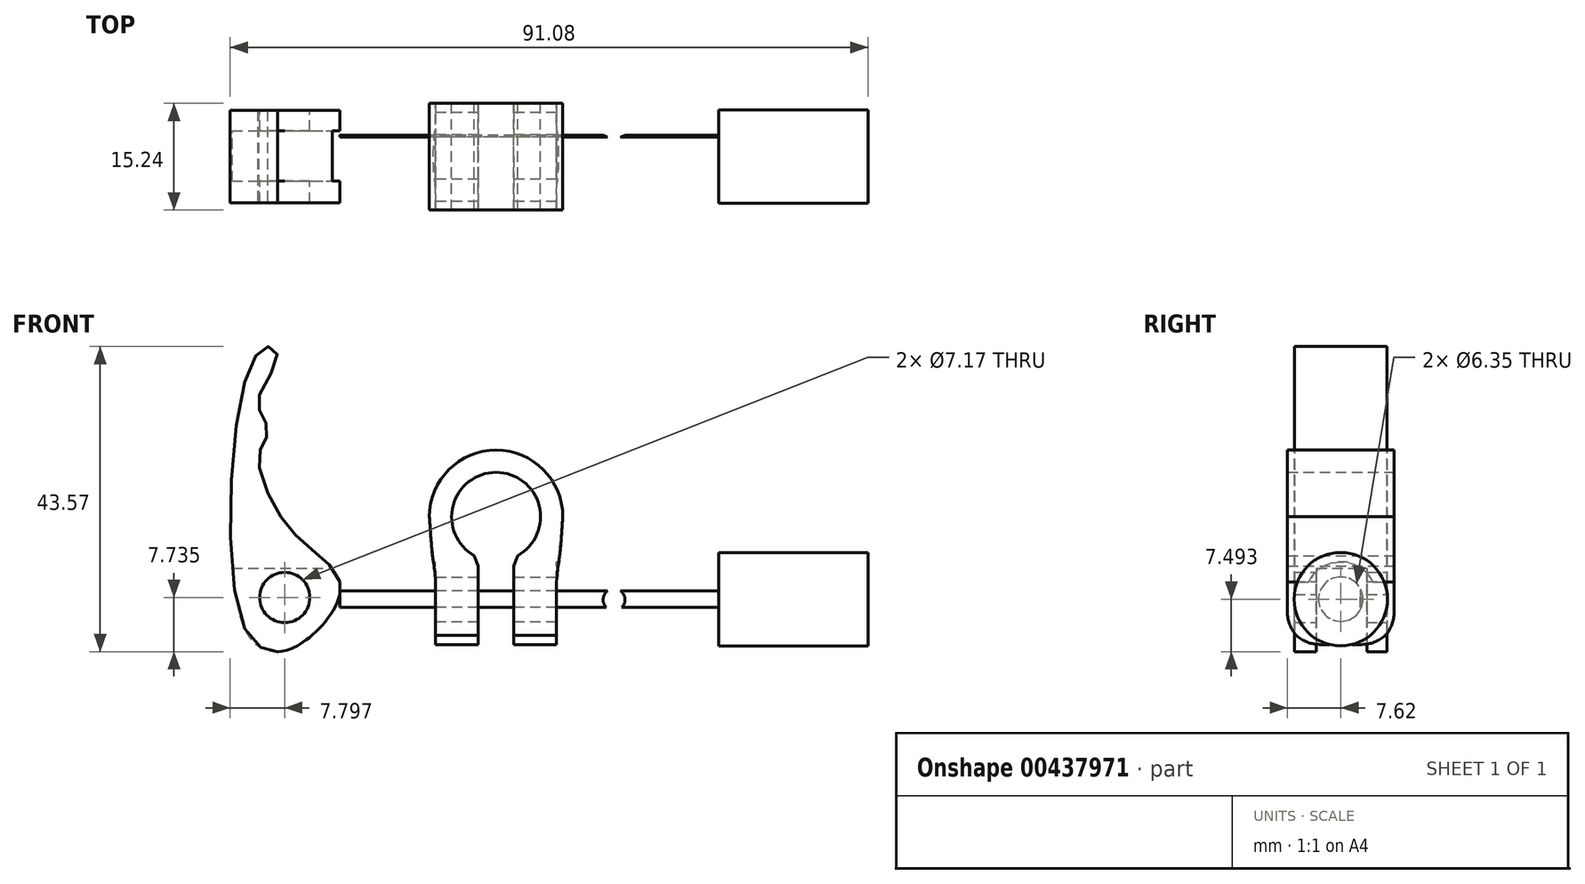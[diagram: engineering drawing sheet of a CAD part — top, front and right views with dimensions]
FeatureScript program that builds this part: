
annotation { "Feature Type Name" : "Feature", "Feature Type Description" : "" }
export const myFeature = defineFeature(function(context is Context, id is Id, definition is map)
    precondition{}
    {
        {
            var Q0;
            Q0=qCreatedBy(makeId("Front.planeOp"),FACE);
            var sketch = newSketch(context, id + "F0", { "sketchPlane" : qUnion([Q0])});
            skArc(sketch, "E0", {"start": v(3.1, -5.54) * mm, "mid": v(0, 6.35) * mm, "end": v(-3.1, -5.54) * mm});
            skArc(sketch, "E1", {"start": v(9.53, 0) * mm, "mid": v(0, 9.53) * mm, "end": v(-9.53, 0) * mm});
            skArc(sketch, "E2.MirrorC", {"start": v(-3.1, -5.54) * mm, "mid": v(0, 6.35) * mm, "end": v(3.1, -5.54) * mm});
            skArc(sketch, "E3.MirrorC", {"start": v(-9.53, 0) * mm, "mid": v(0, 9.53) * mm, "end": v(9.53, 0) * mm});
            skPoint(sketch, "E4.start.orphan", {"position": v(-9.53, 0) * mm});
            skPoint(sketch, "E5.MirrorP", {"position": v(9.53, 0) * mm});
            skLineSegment(sketch, "E6", {"start": v(-2.54, -18.23) * mm, "end": v(-2.54, -7.05) * mm});
            skLineSegment(sketch, "E7", {"start": v(-2.54, -7.05) * mm, "end": v(-3.1, -5.54) * mm});
            skFitSpline(sketch, "E8", {"points": [v(-9.53, 0) * mm, v(-9.23, -4.09) * mm, v(-8.93, -6.6) * mm, v(-8.65, -9.3) * mm, v(-8.65, -18.23) * mm], "startDerivative": vector(1.32, -14.79) * mm, "endDerivative": vector(-0.24, -15.12) * mm});
            skLineSegment(sketch, "E9", {"start": v(-8.65, -18.23) * mm, "end": v(-2.54, -18.23) * mm});
            skLineSegment(sketch, "E10", {"start": v(-8.65, -18.23) * mm, "end": v(-8.65, -9.3) * mm});
            skLineSegment(sketch, "E11.trimOffspring", {"start": v(-8.65, -18.23) * mm, "end": v(-8.65, -18.23) * mm});
            skLineSegment(sketch, "E12.MirrorCS", {"start": v(8.65, -18.23) * mm, "end": v(8.65, -9.3) * mm});
            skFitSpline(sketch, "E13.MirrorCS", {"points": [v(9.53, 0) * mm, v(9.23, -4.09) * mm, v(8.93, -6.6) * mm, v(8.65, -9.3) * mm, v(8.65, -18.23) * mm], "startDerivative": vector(-1.32, -14.79) * mm, "endDerivative": vector(0.24, -15.12) * mm});
            skLineSegment(sketch, "E14.MirrorCS", {"start": v(2.54, -18.23) * mm, "end": v(2.54, -7.05) * mm});
            skLineSegment(sketch, "E15.MirrorCS", {"start": v(8.65, -18.23) * mm, "end": v(2.54, -18.23) * mm});
            skLineSegment(sketch, "E16.MirrorCS", {"start": v(2.54, -7.05) * mm, "end": v(3.1, -5.54) * mm});
            skLineSegment(sketch, "E17.MirrorCS", {"start": v(8.65, -18.23) * mm, "end": v(8.65, -18.23) * mm});
            skSolve(sketch);
        }
        {
            var Q0;
            Q0=qSketchRegion(id+"F0",true);
            extrude(context, id + "F1", {"entities" : qUnion([Q0]), "depth" : 15.24 * mm});
        }
        {
            var Q0;
            Q0=makeQuery(id+"F1.opExtrude","SWEPT_FACE",FACE,{"disambiguationData":[OSD([sQuery(id+"F0.wireOp",EDGE,"E10")])]});
            var sketch = newSketch(context, id + "F2", { "sketchPlane" : qUnion([Q0])});
            skCircle(sketch, "E18", {"center": v(7.62, -11.51) * mm, "radius": 5.08 * mm});
            skPoint(sketch, "E19", {"position": v(7.62, -18.23) * mm});
            skSolve(sketch);
        }
        {
            var Q0;
            Q0=qSketchRegion(id+"F2",true);
            extrude(context, id + "F3", {"entities" : qUnion([Q0]), "operationType" : NewBodyOperationType.REMOVE, "depth" : 25.4 * mm});
        }
        {
            var Q0;
            Q0=makeQuery(id+"F1.opExtrude","SWEPT_FACE",FACE,{"disambiguationData":[OSD([sQuery(id+"F0.wireOp",EDGE,"E12.MirrorCS")])]});
            var sketch = newSketch(context, id + "F4", { "sketchPlane" : qUnion([Q0])});
            skCircle(sketch, "E20", {"center": v(-7.62, -11.51) * mm, "radius": 5.08 * mm});
            skPoint(sketch, "E21", {"position": v(-7.62, -18.23) * mm});
            skSolve(sketch);
        }
        {
            var Q0;
            Q0=qSketchRegion(id+"F4",true);
            extrude(context, id + "F5", {"entities" : qUnion([Q0]), "operationType" : NewBodyOperationType.REMOVE, "depth" : 25.4 * mm});
        }
        {
            var Q0;
            {var subQ0=sQuery(id+"F0.wireOp",EDGE,"E12.MirrorCS");Q0=makeQuery(id+"FgcZc90ez0dEVkm_6.boolean.opBoolean","MERGE",FACE,{"derivedFrom":[makeQuery(id+"FEB0VH3t8ekS347_6.boolean.opBoolean","MERGE",FACE,{"derivedFrom":[makeQuery(id+"F5.boolean.opBoolean","MERGE",FACE,{"derivedFrom":[makeQuery(id+"F1.opExtrude","SWEPT_FACE",FACE,{"disambiguationData":[OSD([subQ0])]}),makeQuery(id+"F5.opExtrude","CAP_FACE",FACE,{"disambiguationData":[OSD([sQuery(id+"F4.wireOp",EDGE,"E20")])],"isStart":true})]}),makeQuery(id+"FEB0VH3t8ekS347_6.opExtrude","SWEPT_FACE",FACE,{"disambiguationData":[OSD([subQ0])]})]}),makeQuery(id+"FgcZc90ez0dEVkm_6.opExtrude","SWEPT_FACE",FACE,{"disambiguationData":[OSD([subQ0])]})]});}
            var sketch = newSketch(context, id + "F6", { "sketchPlane" : qUnion([Q0])});
            skCircle(sketch, "E22", {"center": v(-7.62, -11.76) * mm, "radius": 3.18 * mm});
            skPoint(sketch, "E22.centerSnap0", {"position": v(-7.62, -18.23) * mm});
            skSolve(sketch);
        }
        {
            var Q0;
            Q0=qSketchRegion(id+"F6",true);
            extrude(context, id + "F7", {"entities" : qUnion([Q0]), "operationType" : NewBodyOperationType.REMOVE, "oppositeDirection" : true, "depth" : 25.4 * mm});
        }
        {
            var Q0;
            Q0=makeQuery(id+"F1.opExtrude","CAP_EDGE",EDGE,{"disambiguationData":[OSD([sQuery(id+"F0.wireOp",EDGE,"E15.MirrorCS")])],"isStart":false});
            var Q1;
            Q1=makeQuery(id+"F1.opExtrude","CAP_EDGE",EDGE,{"disambiguationData":[OSD([sQuery(id+"F0.wireOp",EDGE,"E15.MirrorCS")])],"isStart":true});
            var Q2;
            Q2=makeQuery(id+"F1.opExtrude","CAP_EDGE",EDGE,{"disambiguationData":[OSD([sQuery(id+"F0.wireOp",EDGE,"E9")])],"isStart":false});
            var Q3;
            Q3=makeQuery(id+"F1.opExtrude","CAP_EDGE",EDGE,{"disambiguationData":[OSD([sQuery(id+"F0.wireOp",EDGE,"E9")])],"isStart":true});
            chamfer(context, id + "F8", {"entities" : qUnion([Q0, Q1, Q2, Q3]), "width" : 2.54 * mm, "tangentPropagation" : true});
        }
        {
            var Q0;
            {var subQ0=sQuery(id+"F0.wireOp",EDGE,"E9");Q0=makeQuery(id+"F8.opChamfer","BLEND_EDGE",EDGE,{"blendedFrom":[makeQuery(id+"F1.opExtrude","CAP_EDGE",EDGE,{"disambiguationData":[OSD([subQ0])],"isStart":false}),makeQuery(id+"F1.opExtrude","CAP_FACE",FACE,{"disambiguationData":[OSD([sQuery(id+"F0.wireOp",EDGE,"E0"),sQuery(id+"F0.wireOp",EDGE,"E1"),sQuery(id+"F0.wireOp",EDGE,"E6"),sQuery(id+"F0.wireOp",EDGE,"E7"),sQuery(id+"F0.wireOp",EDGE,"E8"),subQ0,sQuery(id+"F0.wireOp",EDGE,"E10"),sQuery(id+"F0.wireOp",EDGE,"E12.MirrorCS"),sQuery(id+"F0.wireOp",EDGE,"E13.MirrorCS"),sQuery(id+"F0.wireOp",EDGE,"E14.MirrorCS"),sQuery(id+"F0.wireOp",EDGE,"E15.MirrorCS"),sQuery(id+"F0.wireOp",EDGE,"E16.MirrorCS")])],"isStart":false})],"blendedInto":[makeQuery(id+"F1.opExtrude","CAP_FACE",FACE,{"disambiguationData":[OSD([sQuery(id+"F0.wireOp",EDGE,"E0"),sQuery(id+"F0.wireOp",EDGE,"E1"),sQuery(id+"F0.wireOp",EDGE,"E6"),sQuery(id+"F0.wireOp",EDGE,"E7"),sQuery(id+"F0.wireOp",EDGE,"E8"),subQ0,sQuery(id+"F0.wireOp",EDGE,"E10"),sQuery(id+"F0.wireOp",EDGE,"E12.MirrorCS"),sQuery(id+"F0.wireOp",EDGE,"E13.MirrorCS"),sQuery(id+"F0.wireOp",EDGE,"E14.MirrorCS"),sQuery(id+"F0.wireOp",EDGE,"E15.MirrorCS"),sQuery(id+"F0.wireOp",EDGE,"E16.MirrorCS")])],"isStart":false})]});}
            var Q1;
            {var subQ0=sQuery(id+"F0.wireOp",EDGE,"E9");Q1=makeQuery(id+"F8.opChamfer","BLEND_EDGE",EDGE,{"blendedFrom":[makeQuery(id+"F1.opExtrude","CAP_EDGE",EDGE,{"disambiguationData":[OSD([subQ0])],"isStart":false}),makeQuery(id+"F1.opExtrude","SWEPT_FACE",FACE,{"disambiguationData":[OSD([subQ0])]})],"blendedInto":[makeQuery(id+"F1.opExtrude","SWEPT_FACE",FACE,{"disambiguationData":[OSD([subQ0])]})]});}
            var Q2;
            {var subQ0=sQuery(id+"F0.wireOp",EDGE,"E9");Q2=makeQuery(id+"F8.opChamfer","BLEND_EDGE",EDGE,{"blendedFrom":[makeQuery(id+"F1.opExtrude","CAP_EDGE",EDGE,{"disambiguationData":[OSD([subQ0])],"isStart":true}),makeQuery(id+"F1.opExtrude","SWEPT_FACE",FACE,{"disambiguationData":[OSD([subQ0])]})],"blendedInto":[makeQuery(id+"F1.opExtrude","SWEPT_FACE",FACE,{"disambiguationData":[OSD([subQ0])]})]});}
            var Q3;
            {var subQ0=sQuery(id+"F0.wireOp",EDGE,"E9");Q3=makeQuery(id+"F8.opChamfer","BLEND_EDGE",EDGE,{"blendedFrom":[makeQuery(id+"F1.opExtrude","CAP_EDGE",EDGE,{"disambiguationData":[OSD([subQ0])],"isStart":true}),makeQuery(id+"F1.opExtrude","CAP_FACE",FACE,{"disambiguationData":[OSD([sQuery(id+"F0.wireOp",EDGE,"E0"),sQuery(id+"F0.wireOp",EDGE,"E1"),sQuery(id+"F0.wireOp",EDGE,"E6"),sQuery(id+"F0.wireOp",EDGE,"E7"),sQuery(id+"F0.wireOp",EDGE,"E8"),subQ0,sQuery(id+"F0.wireOp",EDGE,"E10"),sQuery(id+"F0.wireOp",EDGE,"E12.MirrorCS"),sQuery(id+"F0.wireOp",EDGE,"E13.MirrorCS"),sQuery(id+"F0.wireOp",EDGE,"E14.MirrorCS"),sQuery(id+"F0.wireOp",EDGE,"E15.MirrorCS"),sQuery(id+"F0.wireOp",EDGE,"E16.MirrorCS")])],"isStart":true})],"blendedInto":[makeQuery(id+"F1.opExtrude","CAP_FACE",FACE,{"disambiguationData":[OSD([sQuery(id+"F0.wireOp",EDGE,"E0"),sQuery(id+"F0.wireOp",EDGE,"E1"),sQuery(id+"F0.wireOp",EDGE,"E6"),sQuery(id+"F0.wireOp",EDGE,"E7"),sQuery(id+"F0.wireOp",EDGE,"E8"),subQ0,sQuery(id+"F0.wireOp",EDGE,"E10"),sQuery(id+"F0.wireOp",EDGE,"E12.MirrorCS"),sQuery(id+"F0.wireOp",EDGE,"E13.MirrorCS"),sQuery(id+"F0.wireOp",EDGE,"E14.MirrorCS"),sQuery(id+"F0.wireOp",EDGE,"E15.MirrorCS"),sQuery(id+"F0.wireOp",EDGE,"E16.MirrorCS")])],"isStart":true})]});}
            var Q4;
            {var subQ0=sQuery(id+"F0.wireOp",EDGE,"E15.MirrorCS");Q4=makeQuery(id+"F8.opChamfer","BLEND_EDGE",EDGE,{"blendedFrom":[makeQuery(id+"F1.opExtrude","CAP_EDGE",EDGE,{"disambiguationData":[OSD([subQ0])],"isStart":true}),makeQuery(id+"F1.opExtrude","CAP_FACE",FACE,{"disambiguationData":[OSD([sQuery(id+"F0.wireOp",EDGE,"E0"),sQuery(id+"F0.wireOp",EDGE,"E1"),sQuery(id+"F0.wireOp",EDGE,"E6"),sQuery(id+"F0.wireOp",EDGE,"E7"),sQuery(id+"F0.wireOp",EDGE,"E8"),sQuery(id+"F0.wireOp",EDGE,"E9"),sQuery(id+"F0.wireOp",EDGE,"E10"),sQuery(id+"F0.wireOp",EDGE,"E12.MirrorCS"),sQuery(id+"F0.wireOp",EDGE,"E13.MirrorCS"),sQuery(id+"F0.wireOp",EDGE,"E14.MirrorCS"),subQ0,sQuery(id+"F0.wireOp",EDGE,"E16.MirrorCS")])],"isStart":true})],"blendedInto":[makeQuery(id+"F1.opExtrude","CAP_FACE",FACE,{"disambiguationData":[OSD([sQuery(id+"F0.wireOp",EDGE,"E0"),sQuery(id+"F0.wireOp",EDGE,"E1"),sQuery(id+"F0.wireOp",EDGE,"E6"),sQuery(id+"F0.wireOp",EDGE,"E7"),sQuery(id+"F0.wireOp",EDGE,"E8"),sQuery(id+"F0.wireOp",EDGE,"E9"),sQuery(id+"F0.wireOp",EDGE,"E10"),sQuery(id+"F0.wireOp",EDGE,"E12.MirrorCS"),sQuery(id+"F0.wireOp",EDGE,"E13.MirrorCS"),sQuery(id+"F0.wireOp",EDGE,"E14.MirrorCS"),subQ0,sQuery(id+"F0.wireOp",EDGE,"E16.MirrorCS")])],"isStart":true})]});}
            var Q5;
            {var subQ0=sQuery(id+"F0.wireOp",EDGE,"E15.MirrorCS");Q5=makeQuery(id+"F8.opChamfer","BLEND_EDGE",EDGE,{"blendedFrom":[makeQuery(id+"F1.opExtrude","CAP_EDGE",EDGE,{"disambiguationData":[OSD([subQ0])],"isStart":true}),makeQuery(id+"F1.opExtrude","SWEPT_FACE",FACE,{"disambiguationData":[OSD([subQ0])]})],"blendedInto":[makeQuery(id+"F1.opExtrude","SWEPT_FACE",FACE,{"disambiguationData":[OSD([subQ0])]})]});}
            var Q6;
            {var subQ0=sQuery(id+"F0.wireOp",EDGE,"E15.MirrorCS");Q6=makeQuery(id+"F8.opChamfer","BLEND_EDGE",EDGE,{"blendedFrom":[makeQuery(id+"F1.opExtrude","CAP_EDGE",EDGE,{"disambiguationData":[OSD([subQ0])],"isStart":false}),makeQuery(id+"F1.opExtrude","SWEPT_FACE",FACE,{"disambiguationData":[OSD([subQ0])]})],"blendedInto":[makeQuery(id+"F1.opExtrude","SWEPT_FACE",FACE,{"disambiguationData":[OSD([subQ0])]})]});}
            var Q7;
            {var subQ0=sQuery(id+"F0.wireOp",EDGE,"E15.MirrorCS");Q7=makeQuery(id+"F8.opChamfer","BLEND_EDGE",EDGE,{"blendedFrom":[makeQuery(id+"F1.opExtrude","CAP_EDGE",EDGE,{"disambiguationData":[OSD([subQ0])],"isStart":false}),makeQuery(id+"F1.opExtrude","CAP_FACE",FACE,{"disambiguationData":[OSD([sQuery(id+"F0.wireOp",EDGE,"E0"),sQuery(id+"F0.wireOp",EDGE,"E1"),sQuery(id+"F0.wireOp",EDGE,"E6"),sQuery(id+"F0.wireOp",EDGE,"E7"),sQuery(id+"F0.wireOp",EDGE,"E8"),sQuery(id+"F0.wireOp",EDGE,"E9"),sQuery(id+"F0.wireOp",EDGE,"E10"),sQuery(id+"F0.wireOp",EDGE,"E12.MirrorCS"),sQuery(id+"F0.wireOp",EDGE,"E13.MirrorCS"),sQuery(id+"F0.wireOp",EDGE,"E14.MirrorCS"),subQ0,sQuery(id+"F0.wireOp",EDGE,"E16.MirrorCS")])],"isStart":false})],"blendedInto":[makeQuery(id+"F1.opExtrude","CAP_FACE",FACE,{"disambiguationData":[OSD([sQuery(id+"F0.wireOp",EDGE,"E0"),sQuery(id+"F0.wireOp",EDGE,"E1"),sQuery(id+"F0.wireOp",EDGE,"E6"),sQuery(id+"F0.wireOp",EDGE,"E7"),sQuery(id+"F0.wireOp",EDGE,"E8"),sQuery(id+"F0.wireOp",EDGE,"E9"),sQuery(id+"F0.wireOp",EDGE,"E10"),sQuery(id+"F0.wireOp",EDGE,"E12.MirrorCS"),sQuery(id+"F0.wireOp",EDGE,"E13.MirrorCS"),sQuery(id+"F0.wireOp",EDGE,"E14.MirrorCS"),subQ0,sQuery(id+"F0.wireOp",EDGE,"E16.MirrorCS")])],"isStart":false})]});}
            fillet(context, id + "F9", {"entities" : qUnion([Q0, Q1, Q2, Q3, Q4, Q5, Q6, Q7]), "radius" : 5.08 * mm, "tangentPropagation" : true, "allowEdgeOverflow" : false});
        }
        {
            var Q0;
            Q0=makeQuery(id+"F5.boolean.opBoolean","MERGE",FACE,{"derivedFrom":[makeQuery(id+"F1.opExtrude","SWEPT_FACE",FACE,{"disambiguationData":[OSD([sQuery(id+"F0.wireOp",EDGE,"E12.MirrorCS")])]}),makeQuery(id+"F5.opExtrude","CAP_FACE",FACE,{"disambiguationData":[OSD([sQuery(id+"F4.wireOp",EDGE,"E20")])],"isStart":true})]});
            var sketch = newSketch(context, id + "F10", { "sketchPlane" : qUnion([Q0])});
            skCircle(sketch, "E23", {"center": v(-7.62, -11.76) * mm, "radius": 3.05 * mm});
            skLineSegment(sketch, "E24", {"start": v(-4.81, -10.57) * mm, "end": v(-4.81, -13.24) * mm});
            skSolve(sketch);
        }
        {
            var Q0;
            {var subQ0=sQuery(id+"F10.wireOp",EDGE,"E24");var subQ1=sQuery(id+"F10.wireOp",EDGE,"E23");var subQ2=makeQuery(id+"F10.imprint","INTERSECT",VERTEX,{"disambiguationData":[OD(0.0)],"derivedFrom":[subQ1,subQ0]});Q0=makeQuery(id+"F10.imprint","IMPRINT",FACE,{"disambiguationData":[TD([[makeQuery(id+"F10.imprint","IMPRINT",EDGE,{"disambiguationData":[TD([[subQ2,-1.0]])],"derivedFrom":subQ1}),1.0]])]});}
            extrude(context, id + "F11", {"entities" : qUnion([Q0]), "depth" : 44.45 * mm});
        }
        {
            var Q0;
            Q0=makeQuery(id+"F11.opExtrude","CAP_FACE",FACE,{"disambiguationData":[OSD([sQuery(id+"F10.wireOp",EDGE,"E23")])],"isStart":true});
            extrude(context, id + "F12", {"entities" : qUnion([Q0]), "operationType" : NewBodyOperationType.ADD, "depth" : 30.99 * mm});
        }
        {
            var Q0;
            Q0=makeQuery(id+"F12.opExtrude","CAP_FACE",FACE,{"disambiguationData":[OSD([sQuery(id+"F10.wireOp",EDGE,"E23")])],"isStart":false});
            var sketch = newSketch(context, id + "F13", { "sketchPlane" : qUnion([Q0])});
            skLineSegment(sketch, "E25.bottom", {"start": v(1.02, 24.95) * mm, "end": v(14.22, 24.95) * mm});
            skLineSegment(sketch, "E25.top", {"start": v(1.02, -19.25) * mm, "end": v(14.22, -19.25) * mm});
            skLineSegment(sketch, "E25.left", {"start": v(1.02, 24.95) * mm, "end": v(1.02, -19.25) * mm});
            skLineSegment(sketch, "E25.right", {"start": v(14.22, 24.95) * mm, "end": v(14.22, -19.25) * mm});
            skLineSegment(sketch, "E26.bottom", {"start": v(3.9, -19.25) * mm, "end": v(11.12, -19.25) * mm});
            skLineSegment(sketch, "E26.top", {"start": v(3.9, -7.36) * mm, "end": v(11.12, -7.36) * mm});
            skLineSegment(sketch, "E26.left", {"start": v(3.9, -19.25) * mm, "end": v(3.9, -7.36) * mm});
            skLineSegment(sketch, "E26.right", {"start": v(11.12, -19.25) * mm, "end": v(11.12, -7.36) * mm});
            skSolve(sketch);
        }
        {
            var Q0;
            Q0=makeQuery(id+"F13.imprint","IMPRINT",FACE,{"disambiguationData":[TD([[makeQuery(id+"F13.imprint","IMPRINT",EDGE,{"derivedFrom":sQuery(id+"F13.wireOp",EDGE,"E25.bottom")}),-1.0]])]});
            extrude(context, id + "F14", {"entities" : qUnion([Q0]), "depth" : 17.78 * mm});
        }
        {
            var Q0;
            Q0=makeQuery(id+"F14.opExtrude","SWEPT_FACE",FACE,{"disambiguationData":[OSD([sQuery(id+"F13.wireOp",EDGE,"E25.left")])]});
            var sketch = newSketch(context, id + "F15", { "sketchPlane" : qUnion([Q0])});
            skPoint(sketch, "E27.5.internal.snap0", {"position": v(31.23, -19.25) * mm});
            skPoint(sketch, "E27.10.internal.snap0", {"position": v(31.23, -19.25) * mm});
            skFitSpline(sketch, "E27", {"points": [v(31.23, -19.25) * mm, v(28.62, -18.54) * mm, v(24.27, -14.84) * mm, v(22.34, -9.26) * mm, v(26.41, -4.6) * mm, v(31.23, 0.78) * mm, v(33.89, 8.88) * mm, v(32.77, 11.32) * mm, v(33.19, 14.19) * mm, v(34.02, 16.77) * mm, v(31.23, 22.99) * mm, v(32.63, 24.32) * mm, v(36.33, 17.47) * mm, v(35.7, -16.4) * mm, v(31.23, -19.25) * mm]});
            skCircle(sketch, "E28", {"center": v(30.18, -11.52) * mm, "radius": 3.58 * mm});
            skLineSegment(sketch, "E29", {"start": v(29.96, -5.35) * mm, "end": v(33.78, -2.43) * mm});
            skLineSegment(sketch, "E30", {"start": v(33.78, -2.43) * mm, "end": v(33.78, -6.45) * mm});
            skLineSegment(sketch, "E31", {"start": v(33.78, -6.45) * mm, "end": v(29.96, -5.35) * mm});
            skSolve(sketch);
        }
        {
            var Q0;
            {var subQ0=sQuery(id+"F13.wireOp",EDGE,"E25.left");var subQ1=makeQuery(id+"F14.opExtrude","CAP_EDGE",EDGE,{"disambiguationData":[OSD([subQ0])],"isStart":false});Q0=makeQuery(id+"F15.imprint","IMPRINT",FACE,{"disambiguationData":[TD([[makeQuery(id+"F15.imprint","IMPRINT",EDGE,{"derivedFrom":subQ1}),-1.0]])]});}
            var Q1;
            {var subQ0=sQuery(id+"F15.wireOp",EDGE,"E27");var subQ1=sQuery(id+"F13.wireOp",EDGE,"E25.left");var subQ4=makeQuery(id+"F14.opExtrude","CAP_EDGE",EDGE,{"disambiguationData":[OSD([subQ1])],"isStart":true});var subQ5=makeQuery(id+"F15.imprint","INTERSECT",VERTEX,{"disambiguationData":[OD(0.0)],"derivedFrom":[subQ4,subQ0]});Q1=makeQuery(id+"F15.imprint","IMPRINT",FACE,{"disambiguationData":[TD([[makeQuery(id+"F15.imprint","IMPRINT",EDGE,{"disambiguationData":[TD([[subQ5,1.0]])],"derivedFrom":subQ0}),1.0]])]});}
            var Q2;
            Q2=makeQuery(id+"F15.imprint","IMPRINT",FACE,{"disambiguationData":[TD([[makeQuery(id+"F15.imprint","IMPRINT",EDGE,{"derivedFrom":sQuery(id+"F15.wireOp",EDGE,"E28")}),1.0]])]});
            extrude(context, id + "F16", {"entities" : qUnion([Q0, Q1, Q2]), "operationType" : NewBodyOperationType.REMOVE, "oppositeDirection" : true, "depth" : 25.4 * mm});
        }
        {
            var Q0;
            {var subQ0=sQuery(id+"F10.wireOp",EDGE,"E24");Q0=makeQuery(id+"F12.boolean.opBoolean","MERGE",FACE,{"derivedFrom":[makeQuery(id+"F11.opExtrude","SWEPT_FACE",FACE,{"disambiguationData":[OSD([subQ0])]}),makeQuery(id+"F12.opExtrude","SWEPT_FACE",FACE,{"disambiguationData":[OSD([subQ0])]})]});}
            var sketch = newSketch(context, id + "F17", { "sketchPlane" : qUnion([Q0])});
            skCircle(sketch, "E32", {"center": v(16.85, -11.84) * mm, "radius": 1.57 * mm});
            skSolve(sketch);
        }
        {
            var Q0;
            Q0=qSketchRegion(id+"F17",true);
            extrude(context, id + "F18", {"entities" : qUnion([Q0]), "operationType" : NewBodyOperationType.REMOVE, "oppositeDirection" : true, "depth" : 25.4 * mm});
        }
        {
            var Q0;
            Q0=makeQuery(id+"F11.opExtrude","CAP_FACE",FACE,{"disambiguationData":[OSD([sQuery(id+"F10.wireOp",EDGE,"E23"),sQuery(id+"F10.wireOp",EDGE,"E24")])],"isStart":false});
            var sketch = newSketch(context, id + "F19", { "sketchPlane" : qUnion([Q0])});
            skCircle(sketch, "E33", {"center": v(-7.62, -11.76) * mm, "radius": 6.67 * mm});
            skSolve(sketch);
        }
        {
            var Q0;
            Q0=qSketchRegion(id+"F19",true);
            extrude(context, id + "F20", {"entities" : qUnion([Q0]), "operationType" : NewBodyOperationType.ADD, "oppositeDirection" : true, "depth" : 21.34 * mm});
        }
    });
